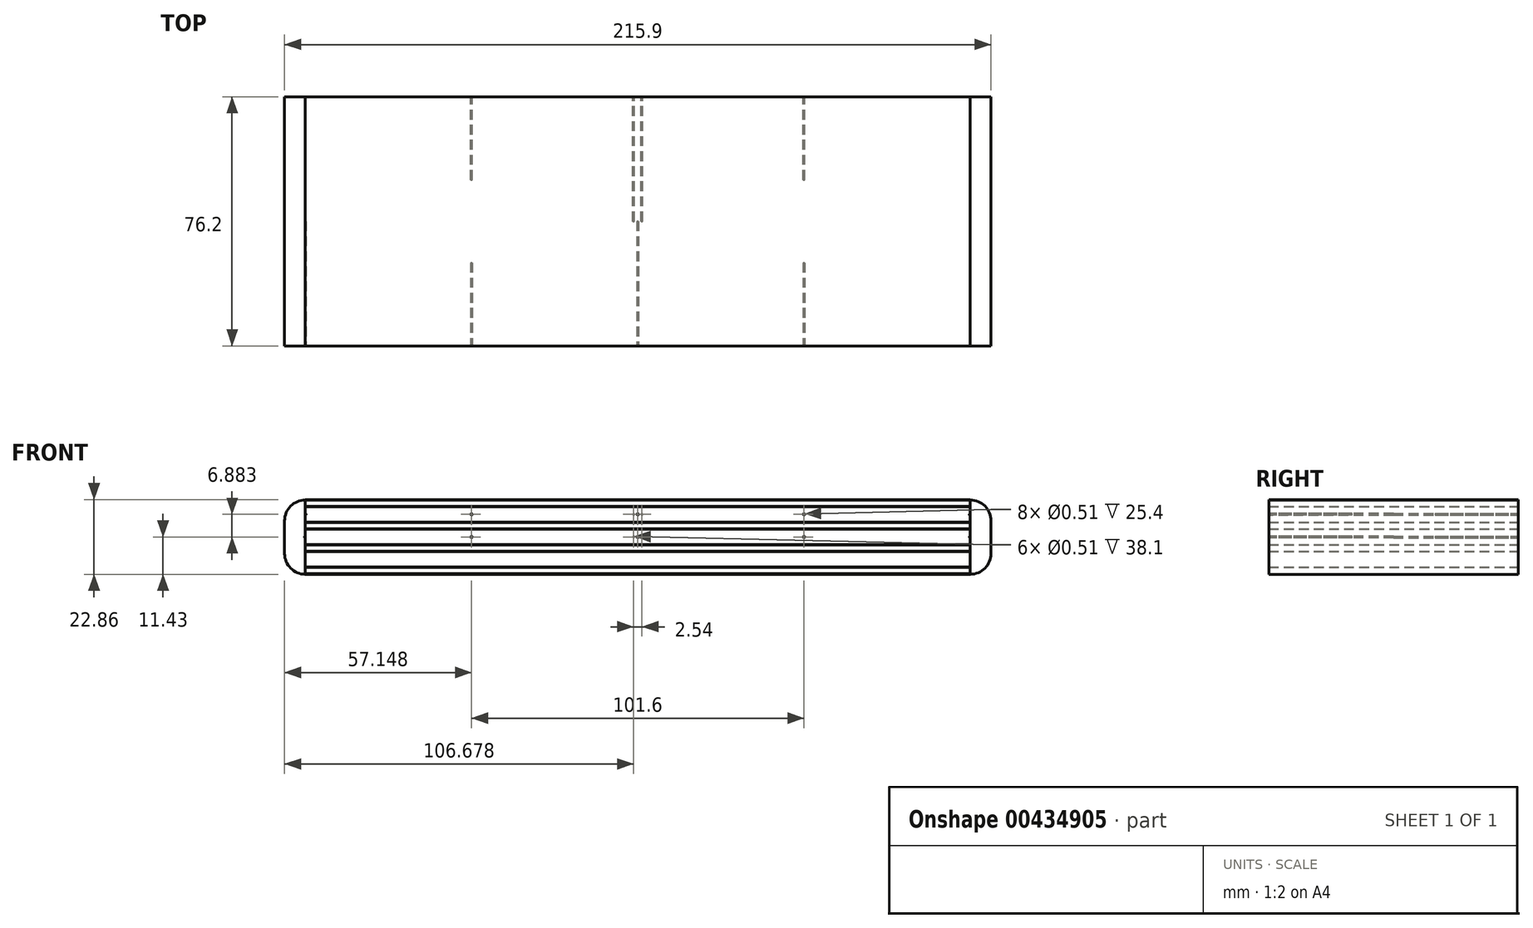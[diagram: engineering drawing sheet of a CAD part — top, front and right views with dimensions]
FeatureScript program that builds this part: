
annotation { "Feature Type Name" : "Feature", "Feature Type Description" : "" }
export const myFeature = defineFeature(function(context is Context, id is Id, definition is map)
    precondition{}
    {
        {
            var Q0;
            Q0=qCreatedBy(makeId("Front.planeOp"),FACE);
            var sketch = newSketch(context, id + "F0", { "sketchPlane" : qUnion([Q0])});
            skPoint(sketch, "E0.middle", {"position": v(0, 0) * mm});
            skLineSegment(sketch, "E1", {"start": v(-40.74, 11.04) * mm, "end": v(162.46, 11.04) * mm});
            skLineSegment(sketch, "E2", {"start": v(-40.74, 11.04) * mm, "end": v(-40.74, -11.82) * mm});
            skLineSegment(sketch, "E3", {"start": v(-40.74, -11.82) * mm, "end": v(162.46, -11.82) * mm});
            skLineSegment(sketch, "E4", {"start": v(162.46, -11.82) * mm, "end": v(162.46, 11.04) * mm});
            skLineSegment(sketch, "E5", {"start": v(0, -11.82) * mm, "end": v(0, -11.67) * mm, "construction": true});
            skLineSegment(sketch, "E6", {"start": v(0, -11.67) * mm, "end": v(0, -9.76) * mm, "construction": true});
            skLineSegment(sketch, "E7", {"start": v(0, -9.76) * mm, "end": v(0, -9.61) * mm, "construction": true});
            skLineSegment(sketch, "E8", {"start": v(0, -9.61) * mm, "end": v(0, -4.94) * mm, "construction": true});
            skLineSegment(sketch, "E9", {"start": v(0, -4.94) * mm, "end": v(0, -4.78) * mm, "construction": true});
            skPoint(sketch, "E9.endSnap0", {"position": v(0, -7.27) * mm});
            skLineSegment(sketch, "E10", {"start": v(0, -4.78) * mm, "end": v(0, -2.88) * mm, "construction": true});
            skLineSegment(sketch, "E11", {"start": v(0, -2.88) * mm, "end": v(0, -2.73) * mm, "construction": true});
            skLineSegment(sketch, "E12", {"start": v(0, -2.73) * mm, "end": v(0, 1.95) * mm, "construction": true});
            skLineSegment(sketch, "E13", {"start": v(0, 1.95) * mm, "end": v(0, 2.1) * mm, "construction": true});
            skLineSegment(sketch, "E14", {"start": v(0, 2.1) * mm, "end": v(0, 4) * mm, "construction": true});
            skLineSegment(sketch, "E15", {"start": v(0, 4) * mm, "end": v(0, 4.16) * mm, "construction": true});
            skLineSegment(sketch, "E16", {"start": v(0, 4.16) * mm, "end": v(0, 8.83) * mm, "construction": true});
            skLineSegment(sketch, "E17", {"start": v(0, 8.83) * mm, "end": v(0, 8.98) * mm, "construction": true});
            skLineSegment(sketch, "E18", {"start": v(0, 8.98) * mm, "end": v(0, 10.89) * mm, "construction": true});
            skLineSegment(sketch, "E19", {"start": v(0, 10.89) * mm, "end": v(0, 11.04) * mm, "construction": true});
            skLineSegment(sketch, "E20", {"start": v(-40.74, -11.67) * mm, "end": v(162.46, -11.67) * mm});
            skLineSegment(sketch, "E21", {"start": v(-40.74, -9.76) * mm, "end": v(162.46, -9.76) * mm});
            skLineSegment(sketch, "E22", {"start": v(-40.74, -9.61) * mm, "end": v(162.46, -9.61) * mm});
            skLineSegment(sketch, "E23", {"start": v(-40.74, -4.94) * mm, "end": v(162.46, -4.94) * mm});
            skLineSegment(sketch, "E24", {"start": v(-40.74, -4.78) * mm, "end": v(162.46, -4.78) * mm});
            skLineSegment(sketch, "E25", {"start": v(-40.74, -2.88) * mm, "end": v(162.46, -2.88) * mm});
            skLineSegment(sketch, "E26", {"start": v(-40.74, -2.73) * mm, "end": v(162.46, -2.73) * mm});
            skLineSegment(sketch, "E27", {"start": v(-40.74, 1.95) * mm, "end": v(162.46, 1.95) * mm});
            skLineSegment(sketch, "E28", {"start": v(-40.74, 2.1) * mm, "end": v(162.46, 2.1) * mm});
            skLineSegment(sketch, "E29", {"start": v(-40.74, 4) * mm, "end": v(162.46, 4) * mm});
            skLineSegment(sketch, "E30", {"start": v(-40.74, 4.16) * mm, "end": v(162.46, 4.16) * mm});
            skLineSegment(sketch, "E31", {"start": v(-40.74, 8.83) * mm, "end": v(162.46, 8.83) * mm});
            skLineSegment(sketch, "E32", {"start": v(-40.74, 8.98) * mm, "end": v(162.46, 8.98) * mm});
            skLineSegment(sketch, "E33", {"start": v(-40.74, 10.89) * mm, "end": v(162.46, 10.89) * mm});
            skSolve(sketch);
        }
        {
            var Q0;
            {var subQ0=sQuery(id+"F0.wireOp",EDGE,"E3");Q0=makeQuery(id+"F0.imprint","IMPRINT",FACE,{"disambiguationData":[TD([[makeQuery(id+"F0.imprint","IMPRINT",EDGE,{"derivedFrom":subQ0}),1.0]])]});}
            var Q1;
            {var subQ0=sQuery(id+"F0.wireOp",EDGE,"E21");Q1=makeQuery(id+"F0.imprint","IMPRINT",FACE,{"disambiguationData":[TD([[makeQuery(id+"F0.imprint","IMPRINT",EDGE,{"derivedFrom":subQ0}),1.0]])]});}
            var Q2;
            {var subQ0=sQuery(id+"F0.wireOp",EDGE,"E23");Q2=makeQuery(id+"F0.imprint","IMPRINT",FACE,{"disambiguationData":[TD([[makeQuery(id+"F0.imprint","IMPRINT",EDGE,{"derivedFrom":subQ0}),1.0]])]});}
            var Q3;
            {var subQ0=sQuery(id+"F0.wireOp",EDGE,"E25");Q3=makeQuery(id+"F0.imprint","IMPRINT",FACE,{"disambiguationData":[TD([[makeQuery(id+"F0.imprint","IMPRINT",EDGE,{"derivedFrom":subQ0}),1.0]])]});}
            var Q4;
            {var subQ0=sQuery(id+"F0.wireOp",EDGE,"E27");Q4=makeQuery(id+"F0.imprint","IMPRINT",FACE,{"disambiguationData":[TD([[makeQuery(id+"F0.imprint","IMPRINT",EDGE,{"derivedFrom":subQ0}),1.0]])]});}
            var Q5;
            {var subQ0=sQuery(id+"F0.wireOp",EDGE,"E29");Q5=makeQuery(id+"F0.imprint","IMPRINT",FACE,{"disambiguationData":[TD([[makeQuery(id+"F0.imprint","IMPRINT",EDGE,{"derivedFrom":subQ0}),1.0]])]});}
            var Q6;
            {var subQ0=sQuery(id+"F0.wireOp",EDGE,"E31");Q6=makeQuery(id+"F0.imprint","IMPRINT",FACE,{"disambiguationData":[TD([[makeQuery(id+"F0.imprint","IMPRINT",EDGE,{"derivedFrom":subQ0}),1.0]])]});}
            var Q7;
            {var subQ0=sQuery(id+"F0.wireOp",EDGE,"E1");Q7=makeQuery(id+"F0.imprint","IMPRINT",FACE,{"disambiguationData":[TD([[makeQuery(id+"F0.imprint","IMPRINT",EDGE,{"derivedFrom":subQ0}),-1.0]])]});}
            extrude(context, id + "F1", {"entities" : qUnion([Q0, Q1, Q2, Q3, Q4, Q5, Q6, Q7]), "depth" : 76.2 * mm});
        }
        {
            var Q0;
            {var subQ0=sQuery(id+"F0.wireOp",EDGE,"E20");Q0=makeQuery(id+"F0.imprint","IMPRINT",FACE,{"disambiguationData":[TD([[makeQuery(id+"F0.imprint","IMPRINT",EDGE,{"derivedFrom":subQ0}),1.0]])]});}
            var Q1;
            {var subQ0=sQuery(id+"F0.wireOp",EDGE,"E24");Q1=makeQuery(id+"F0.imprint","IMPRINT",FACE,{"disambiguationData":[TD([[makeQuery(id+"F0.imprint","IMPRINT",EDGE,{"derivedFrom":subQ0}),1.0]])]});}
            var Q2;
            {var subQ0=sQuery(id+"F0.wireOp",EDGE,"E28");Q2=makeQuery(id+"F0.imprint","IMPRINT",FACE,{"disambiguationData":[TD([[makeQuery(id+"F0.imprint","IMPRINT",EDGE,{"derivedFrom":subQ0}),1.0]])]});}
            var Q3;
            {var subQ0=sQuery(id+"F0.wireOp",EDGE,"E32");Q3=makeQuery(id+"F0.imprint","IMPRINT",FACE,{"disambiguationData":[TD([[makeQuery(id+"F0.imprint","IMPRINT",EDGE,{"derivedFrom":subQ0}),1.0]])]});}
            extrude(context, id + "F2", {"entities" : qUnion([Q0, Q1, Q2, Q3]), "depth" : 76.2 * mm});
        }
        {
            var Q0;
            {var subQ0=sQuery(id+"F0.wireOp",EDGE,"E30");Q0=makeQuery(id+"F0.imprint","IMPRINT",FACE,{"disambiguationData":[TD([[makeQuery(id+"F0.imprint","IMPRINT",EDGE,{"derivedFrom":subQ0}),1.0]])]});}
            var Q1;
            {var subQ0=sQuery(id+"F0.wireOp",EDGE,"E26");Q1=makeQuery(id+"F0.imprint","IMPRINT",FACE,{"disambiguationData":[TD([[makeQuery(id+"F0.imprint","IMPRINT",EDGE,{"derivedFrom":subQ0}),1.0]])]});}
            var Q2;
            {var subQ0=sQuery(id+"F0.wireOp",EDGE,"E22");Q2=makeQuery(id+"F0.imprint","IMPRINT",FACE,{"disambiguationData":[TD([[makeQuery(id+"F0.imprint","IMPRINT",EDGE,{"derivedFrom":subQ0}),1.0]])]});}
            extrude(context, id + "F3", {"entities" : qUnion([Q0, Q1, Q2]), "depth" : 76.2 * mm});
        }
        {
            var Q0;
            {var subQ0=sQuery(id+"F0.wireOp",EDGE,"E4");Q0=makeQuery(id+"F1.opExtrude","SWEPT_FACE",FACE,{"disambiguationData":[OSD([subQ0]),TDD([makeQuery(id+"F0.imprint","IMPRINT",EDGE,{"disambiguationData":[TD([[makeQuery(id+"F0.imprint","INTERSECT",VERTEX,{"derivedFrom":[sQuery(id+"F0.wireOp",EDGE,"E1"),subQ0]}),1.0]])],"derivedFrom":subQ0})])]});}
            var sketch = newSketch(context, id + "F4", { "sketchPlane" : qUnion([Q0])});
            skLineSegment(sketch, "E34.bottom", {"start": v(-76.2, 11.04) * mm, "end": v(0, 11.04) * mm});
            skLineSegment(sketch, "E34.top", {"start": v(-76.2, -11.82) * mm, "end": v(0, -11.82) * mm});
            skLineSegment(sketch, "E34.left", {"start": v(-76.2, 11.04) * mm, "end": v(-76.2, -11.82) * mm});
            skLineSegment(sketch, "E34.right", {"start": v(0, 11.04) * mm, "end": v(0, -11.82) * mm});
            skSolve(sketch);
        }
        {
            var Q0;
            {var subQ0=sQuery(id+"F4.wireOp",EDGE,"E34.top");Q0=makeQuery(id+"F4.imprint","IMPRINT",FACE,{"disambiguationData":[TD([[makeQuery(id+"F4.imprint","IMPRINT",EDGE,{"derivedFrom":subQ0}),1.0]])]});}
            extrude(context, id + "F5", {"entities" : qUnion([Q0]), "depth" : 6.35 * mm});
        }
        {
            var Q0;
            {var subQ0=sQuery(id+"F0.wireOp",EDGE,"E2");Q0=makeQuery(id+"F1.opExtrude","SWEPT_FACE",FACE,{"disambiguationData":[OSD([subQ0]),TDD([makeQuery(id+"F0.imprint","IMPRINT",EDGE,{"disambiguationData":[TD([[makeQuery(id+"F0.imprint","INTERSECT",VERTEX,{"derivedFrom":[sQuery(id+"F0.wireOp",EDGE,"E1"),subQ0]}),-1.0]])],"derivedFrom":subQ0})])]});}
            var sketch = newSketch(context, id + "F6", { "sketchPlane" : qUnion([Q0])});
            skLineSegment(sketch, "E35.bottom", {"start": v(0, 11.04) * mm, "end": v(76.2, 11.04) * mm});
            skLineSegment(sketch, "E35.top", {"start": v(0, -11.82) * mm, "end": v(76.2, -11.82) * mm});
            skLineSegment(sketch, "E35.left", {"start": v(0, 11.04) * mm, "end": v(0, -11.82) * mm});
            skLineSegment(sketch, "E35.right", {"start": v(76.2, 11.04) * mm, "end": v(76.2, -11.82) * mm});
            skSolve(sketch);
        }
        {
            var Q0;
            {var subQ0=sQuery(id+"F6.wireOp",EDGE,"E35.top");Q0=makeQuery(id+"F6.imprint","IMPRINT",FACE,{"disambiguationData":[TD([[makeQuery(id+"F6.imprint","IMPRINT",EDGE,{"derivedFrom":subQ0}),1.0]])]});}
            extrude(context, id + "F7", {"entities" : qUnion([Q0]), "depth" : 6.35 * mm});
        }
        {
            var Q0;
            Q0=makeQuery(id+"F3.opExtrude","CAP_FACE",FACE,{"disambiguationData":[OSD([sQuery(id+"F0.wireOp",EDGE,"E2"),sQuery(id+"F0.wireOp",EDGE,"E4"),sQuery(id+"F0.wireOp",EDGE,"E26"),sQuery(id+"F0.wireOp",EDGE,"E27")])],"isStart":false});
            var sketch = newSketch(context, id + "F8", { "sketchPlane" : qUnion([Q0])});
            skCircle(sketch, "E36", {"center": v(-40.74, -0.4) * mm, "radius": 0.25 * mm});
            skLineSegment(sketch, "E37", {"start": v(-40.74, -0.4) * mm, "end": v(10.06, -0.4) * mm, "construction": true});
            skLineSegment(sketch, "E38", {"start": v(10.06, -0.4) * mm, "end": v(60.86, -0.4) * mm, "construction": true});
            skLineSegment(sketch, "E39", {"start": v(60.86, -0.4) * mm, "end": v(111.66, -0.4) * mm, "construction": true});
            skLineSegment(sketch, "E40", {"start": v(111.66, -0.4) * mm, "end": v(162.46, -0.4) * mm, "construction": true});
            skCircle(sketch, "E41", {"center": v(10.06, -0.4) * mm, "radius": 0.25 * mm});
            skCircle(sketch, "E42", {"center": v(60.86, -0.4) * mm, "radius": 0.25 * mm});
            skCircle(sketch, "E43", {"center": v(111.66, -0.4) * mm, "radius": 0.25 * mm});
            skCircle(sketch, "E44", {"center": v(162.46, -0.4) * mm, "radius": 0.25 * mm});
            skSolve(sketch);
        }
        {
            var Q0;
            {var subQ0=sQuery(id+"F8.wireOp",EDGE,"E36");var subQ1=sQuery(id+"F0.wireOp",EDGE,"E2");var subQ2=makeQuery(id+"F3.opExtrude","CAP_EDGE",EDGE,{"disambiguationData":[OSD([subQ1]),TDD([makeQuery(id+"F0.imprint","IMPRINT",EDGE,{"disambiguationData":[TD([[makeQuery(id+"F0.imprint","INTERSECT",VERTEX,{"derivedFrom":[subQ1,sQuery(id+"F0.wireOp",EDGE,"E26")]}),1.0]])],"derivedFrom":subQ1})])],"isStart":false});var subQ3=makeQuery(id+"F8.imprint","INTERSECT",VERTEX,{"disambiguationData":[OD(0.0)],"derivedFrom":[subQ2,subQ0]});Q0=makeQuery(id+"F8.imprint","IMPRINT",FACE,{"disambiguationData":[TD([[makeQuery(id+"F8.imprint","IMPRINT",EDGE,{"disambiguationData":[TD([[subQ3,-1.0]])],"derivedFrom":subQ0}),1.0]])]});}
            var Q1;
            Q1=makeQuery(id+"F8.imprint","IMPRINT",FACE,{"disambiguationData":[TD([[makeQuery(id+"F8.imprint","IMPRINT",EDGE,{"derivedFrom":sQuery(id+"F8.wireOp",EDGE,"E42")}),1.0]])]});
            var Q2;
            {var subQ0=sQuery(id+"F8.wireOp",EDGE,"E44");var subQ1=sQuery(id+"F0.wireOp",EDGE,"E4");var subQ2=makeQuery(id+"F3.opExtrude","CAP_EDGE",EDGE,{"disambiguationData":[OSD([subQ1]),TDD([makeQuery(id+"F0.imprint","IMPRINT",EDGE,{"disambiguationData":[TD([[makeQuery(id+"F0.imprint","INTERSECT",VERTEX,{"derivedFrom":[subQ1,sQuery(id+"F0.wireOp",EDGE,"E26")]}),-1.0]])],"derivedFrom":subQ1})])],"isStart":false});var subQ3=makeQuery(id+"F8.imprint","INTERSECT",VERTEX,{"disambiguationData":[OD(0.0)],"derivedFrom":[subQ2,subQ0]});Q2=makeQuery(id+"F8.imprint","IMPRINT",FACE,{"disambiguationData":[TD([[makeQuery(id+"F8.imprint","IMPRINT",EDGE,{"disambiguationData":[TD([[subQ3,1.0]])],"derivedFrom":subQ0}),1.0]])]});}
            extrude(context, id + "F9", {"entities" : qUnion([Q0, Q1, Q2]), "operationType" : NewBodyOperationType.REMOVE, "oppositeDirection" : true, "depth" : 38.1 * mm});
        }
        {
            var Q0;
            Q0=makeQuery(id+"F3.opExtrude","CAP_FACE",FACE,{"disambiguationData":[OSD([sQuery(id+"F0.wireOp",EDGE,"E2"),sQuery(id+"F0.wireOp",EDGE,"E4"),sQuery(id+"F0.wireOp",EDGE,"E30"),sQuery(id+"F0.wireOp",EDGE,"E31")])],"isStart":false});
            var sketch = newSketch(context, id + "F10", { "sketchPlane" : qUnion([Q0])});
            skCircle(sketch, "E45", {"center": v(-40.74, 6.5) * mm, "radius": 0.25 * mm});
            skLineSegment(sketch, "E46", {"start": v(-40.74, 6.5) * mm, "end": v(10.06, 6.5) * mm, "construction": true});
            skLineSegment(sketch, "E47", {"start": v(10.06, 6.5) * mm, "end": v(60.86, 6.5) * mm, "construction": true});
            skLineSegment(sketch, "E48", {"start": v(60.86, 6.5) * mm, "end": v(111.66, 6.5) * mm, "construction": true});
            skLineSegment(sketch, "E49", {"start": v(111.66, 6.5) * mm, "end": v(162.46, 6.4) * mm, "construction": true});
            skCircle(sketch, "E50", {"center": v(10.06, 6.5) * mm, "radius": 0.25 * mm});
            skCircle(sketch, "E51", {"center": v(60.86, 6.5) * mm, "radius": 0.25 * mm});
            skCircle(sketch, "E52", {"center": v(111.66, 6.5) * mm, "radius": 0.25 * mm});
            skCircle(sketch, "E53", {"center": v(162.46, 6.4) * mm, "radius": 0.25 * mm});
            skSolve(sketch);
        }
        {
            var Q0;
            {var subQ0=sQuery(id+"F10.wireOp",EDGE,"E53");var subQ1=sQuery(id+"F0.wireOp",EDGE,"E4");var subQ2=makeQuery(id+"F3.opExtrude","CAP_EDGE",EDGE,{"disambiguationData":[OSD([subQ1]),TDD([makeQuery(id+"F0.imprint","IMPRINT",EDGE,{"disambiguationData":[TD([[makeQuery(id+"F0.imprint","INTERSECT",VERTEX,{"derivedFrom":[subQ1,sQuery(id+"F0.wireOp",EDGE,"E30")]}),-1.0]])],"derivedFrom":subQ1})])],"isStart":false});var subQ3=makeQuery(id+"F10.imprint","INTERSECT",VERTEX,{"disambiguationData":[OD(0.0)],"derivedFrom":[subQ2,subQ0]});Q0=makeQuery(id+"F10.imprint","IMPRINT",FACE,{"disambiguationData":[TD([[makeQuery(id+"F10.imprint","IMPRINT",EDGE,{"disambiguationData":[TD([[subQ3,1.0]])],"derivedFrom":subQ0}),1.0]])]});}
            var Q1;
            Q1=makeQuery(id+"F10.imprint","IMPRINT",FACE,{"disambiguationData":[TD([[makeQuery(id+"F10.imprint","IMPRINT",EDGE,{"derivedFrom":sQuery(id+"F10.wireOp",EDGE,"E51")}),1.0]])]});
            var Q2;
            {var subQ0=sQuery(id+"F10.wireOp",EDGE,"E45");var subQ1=sQuery(id+"F0.wireOp",EDGE,"E2");var subQ2=makeQuery(id+"F3.opExtrude","CAP_EDGE",EDGE,{"disambiguationData":[OSD([subQ1]),TDD([makeQuery(id+"F0.imprint","IMPRINT",EDGE,{"disambiguationData":[TD([[makeQuery(id+"F0.imprint","INTERSECT",VERTEX,{"derivedFrom":[subQ1,sQuery(id+"F0.wireOp",EDGE,"E30")]}),1.0]])],"derivedFrom":subQ1})])],"isStart":false});var subQ3=makeQuery(id+"F10.imprint","INTERSECT",VERTEX,{"disambiguationData":[OD(0.0)],"derivedFrom":[subQ2,subQ0]});Q2=makeQuery(id+"F10.imprint","IMPRINT",FACE,{"disambiguationData":[TD([[makeQuery(id+"F10.imprint","IMPRINT",EDGE,{"disambiguationData":[TD([[subQ3,-1.0]])],"derivedFrom":subQ0}),1.0]])]});}
            extrude(context, id + "F11", {"entities" : qUnion([Q0, Q1, Q2]), "operationType" : NewBodyOperationType.REMOVE, "oppositeDirection" : true, "depth" : 38.1 * mm});
        }
        {
            var Q0;
            Q0=makeQuery(id+"F5.opExtrude","CAP_EDGE",EDGE,{"disambiguationData":[OSD([sQuery(id+"F0.wireOp",EDGE,"E4"),sQuery(id+"F0.wireOp",EDGE,"E33")])],"isStart":false});
            var Q1;
            Q1=makeQuery(id+"F5.opExtrude","CAP_EDGE",EDGE,{"disambiguationData":[OSD([sQuery(id+"F4.wireOp",EDGE,"E34.top")])],"isStart":false});
            var Q2;
            Q2=makeQuery(id+"F7.opExtrude","CAP_EDGE",EDGE,{"disambiguationData":[OSD([sQuery(id+"F6.wireOp",EDGE,"E35.top")])],"isStart":false});
            var Q3;
            Q3=makeQuery(id+"F7.opExtrude","CAP_EDGE",EDGE,{"disambiguationData":[OSD([sQuery(id+"F0.wireOp",EDGE,"E2"),sQuery(id+"F0.wireOp",EDGE,"E33")])],"isStart":false});
            fillet(context, id + "F12", {"entities" : qUnion([Q0, Q1, Q2, Q3]), "radius" : 6.35 * mm, "tangentPropagation" : true, "allowEdgeOverflow" : false});
        }
        {
            var Q0;
            Q0=makeQuery(id+"F8.imprint","IMPRINT",FACE,{"disambiguationData":[TD([[makeQuery(id+"F8.imprint","IMPRINT",EDGE,{"derivedFrom":sQuery(id+"F8.wireOp",EDGE,"E41")}),1.0]])]});
            var Q1;
            Q1=makeQuery(id+"F8.imprint","IMPRINT",FACE,{"disambiguationData":[TD([[makeQuery(id+"F8.imprint","IMPRINT",EDGE,{"derivedFrom":sQuery(id+"F8.wireOp",EDGE,"E43")}),1.0]])]});
            extrude(context, id + "F13", {"entities" : qUnion([Q0, Q1]), "operationType" : NewBodyOperationType.REMOVE, "oppositeDirection" : true, "depth" : 25.4 * mm});
        }
        {
            var Q0;
            Q0=makeQuery(id+"F10.imprint","IMPRINT",FACE,{"disambiguationData":[TD([[makeQuery(id+"F10.imprint","IMPRINT",EDGE,{"derivedFrom":sQuery(id+"F10.wireOp",EDGE,"E50")}),1.0]])]});
            var Q1;
            Q1=makeQuery(id+"F10.imprint","IMPRINT",FACE,{"disambiguationData":[TD([[makeQuery(id+"F10.imprint","IMPRINT",EDGE,{"derivedFrom":sQuery(id+"F10.wireOp",EDGE,"E52")}),1.0]])]});
            extrude(context, id + "F14", {"entities" : qUnion([Q0, Q1]), "operationType" : NewBodyOperationType.REMOVE, "oppositeDirection" : true, "depth" : 25.4 * mm});
        }
        {
            var Q0;
            Q0=makeQuery(id+"F3.opExtrude","CAP_FACE",FACE,{"disambiguationData":[OSD([sQuery(id+"F0.wireOp",EDGE,"E2"),sQuery(id+"F0.wireOp",EDGE,"E4"),sQuery(id+"F0.wireOp",EDGE,"E30"),sQuery(id+"F0.wireOp",EDGE,"E31")])],"isStart":true});
            var sketch = newSketch(context, id + "F15", { "sketchPlane" : qUnion([Q0])});
            skPoint(sketch, "E54.endSnap0", {"position": v(-60.86, 4.16) * mm});
            skLineSegment(sketch, "E55", {"start": v(-60.86, 8.83) * mm, "end": v(-60.86, 6.5) * mm, "construction": true});
            skCircle(sketch, "E56", {"center": v(-60.86, 6.5) * mm, "radius": 0.25 * mm});
            skLineSegment(sketch, "E57", {"start": v(-60.86, 6.5) * mm, "end": v(-10.06, 6.5) * mm, "construction": true});
            skCircle(sketch, "E58", {"center": v(-10.06, 6.5) * mm, "radius": 0.25 * mm});
            skLineSegment(sketch, "E59", {"start": v(-60.86, 6.5) * mm, "end": v(-111.66, 6.5) * mm, "construction": true});
            skCircle(sketch, "E60", {"center": v(-111.66, 6.5) * mm, "radius": 0.25 * mm});
            skLineSegment(sketch, "E61", {"start": v(-60.86, 6.5) * mm, "end": v(-59.59, 6.5) * mm, "construction": true});
            skLineSegment(sketch, "E62", {"start": v(-60.86, 6.5) * mm, "end": v(-62.13, 6.5) * mm, "construction": true});
            skCircle(sketch, "E63", {"center": v(-62.13, 6.5) * mm, "radius": 0.25 * mm});
            skCircle(sketch, "E64", {"center": v(-59.59, 6.5) * mm, "radius": 0.25 * mm});
            skSolve(sketch);
        }
        {
            var Q0;
            Q0=makeQuery(id+"F3.opExtrude","CAP_FACE",FACE,{"disambiguationData":[OSD([sQuery(id+"F0.wireOp",EDGE,"E2"),sQuery(id+"F0.wireOp",EDGE,"E4"),sQuery(id+"F0.wireOp",EDGE,"E26"),sQuery(id+"F0.wireOp",EDGE,"E27")])],"isStart":true});
            var sketch = newSketch(context, id + "F16", { "sketchPlane" : qUnion([Q0])});
            skLineSegment(sketch, "E65", {"start": v(-60.86, 1.95) * mm, "end": v(-60.86, -0.4) * mm, "construction": true});
            skCircle(sketch, "E66", {"center": v(-60.86, -0.4) * mm, "radius": 0.25 * mm});
            skLineSegment(sketch, "E67", {"start": v(-60.86, -0.4) * mm, "end": v(-10.06, -0.4) * mm, "construction": true});
            skLineSegment(sketch, "E68", {"start": v(-60.86, -0.4) * mm, "end": v(-111.66, -0.4) * mm, "construction": true});
            skCircle(sketch, "E69", {"center": v(-10.06, -0.4) * mm, "radius": 0.25 * mm});
            skCircle(sketch, "E70", {"center": v(-111.66, -0.4) * mm, "radius": 0.25 * mm});
            skLineSegment(sketch, "E71", {"start": v(-60.86, -0.4) * mm, "end": v(-59.59, -0.4) * mm, "construction": true});
            skLineSegment(sketch, "E72", {"start": v(-60.86, -0.4) * mm, "end": v(-62.13, -0.4) * mm, "construction": true});
            skCircle(sketch, "E73", {"center": v(-62.13, -0.4) * mm, "radius": 0.25 * mm});
            skCircle(sketch, "E74", {"center": v(-59.59, -0.4) * mm, "radius": 0.25 * mm});
            skSolve(sketch);
        }
        {
            var Q0;
            Q0=makeQuery(id+"F15.imprint","IMPRINT",FACE,{"disambiguationData":[TD([[makeQuery(id+"F15.imprint","IMPRINT",EDGE,{"derivedFrom":sQuery(id+"F15.wireOp",EDGE,"E60")}),1.0]])]});
            var Q1;
            Q1=makeQuery(id+"F16.imprint","IMPRINT",FACE,{"disambiguationData":[TD([[makeQuery(id+"F16.imprint","IMPRINT",EDGE,{"derivedFrom":sQuery(id+"F16.wireOp",EDGE,"E70")}),1.0]])]});
            var Q2;
            Q2=makeQuery(id+"F15.imprint","IMPRINT",FACE,{"disambiguationData":[TD([[makeQuery(id+"F15.imprint","IMPRINT",EDGE,{"derivedFrom":sQuery(id+"F15.wireOp",EDGE,"E58")}),1.0]])]});
            var Q3;
            Q3=makeQuery(id+"F16.imprint","IMPRINT",FACE,{"disambiguationData":[TD([[makeQuery(id+"F16.imprint","IMPRINT",EDGE,{"derivedFrom":sQuery(id+"F16.wireOp",EDGE,"E69")}),1.0]])]});
            extrude(context, id + "F17", {"entities" : qUnion([Q0, Q1, Q2, Q3]), "operationType" : NewBodyOperationType.REMOVE, "oppositeDirection" : true, "depth" : 25.4 * mm});
        }
        {
            var Q0;
            Q0=makeQuery(id+"F16.imprint","IMPRINT",FACE,{"disambiguationData":[TD([[makeQuery(id+"F16.imprint","IMPRINT",EDGE,{"derivedFrom":sQuery(id+"F16.wireOp",EDGE,"E73")}),1.0]])]});
            var Q1;
            Q1=makeQuery(id+"F16.imprint","IMPRINT",FACE,{"disambiguationData":[TD([[makeQuery(id+"F16.imprint","IMPRINT",EDGE,{"derivedFrom":sQuery(id+"F16.wireOp",EDGE,"E74")}),1.0]])]});
            var Q2;
            Q2=makeQuery(id+"F15.imprint","IMPRINT",FACE,{"disambiguationData":[TD([[makeQuery(id+"F15.imprint","IMPRINT",EDGE,{"derivedFrom":sQuery(id+"F15.wireOp",EDGE,"E63")}),1.0]])]});
            var Q3;
            Q3=makeQuery(id+"F15.imprint","IMPRINT",FACE,{"disambiguationData":[TD([[makeQuery(id+"F15.imprint","IMPRINT",EDGE,{"derivedFrom":sQuery(id+"F15.wireOp",EDGE,"E64")}),1.0]])]});
            extrude(context, id + "F18", {"entities" : qUnion([Q0, Q1, Q2, Q3]), "operationType" : NewBodyOperationType.REMOVE, "oppositeDirection" : true, "depth" : 38.1 * mm});
        }
    });
